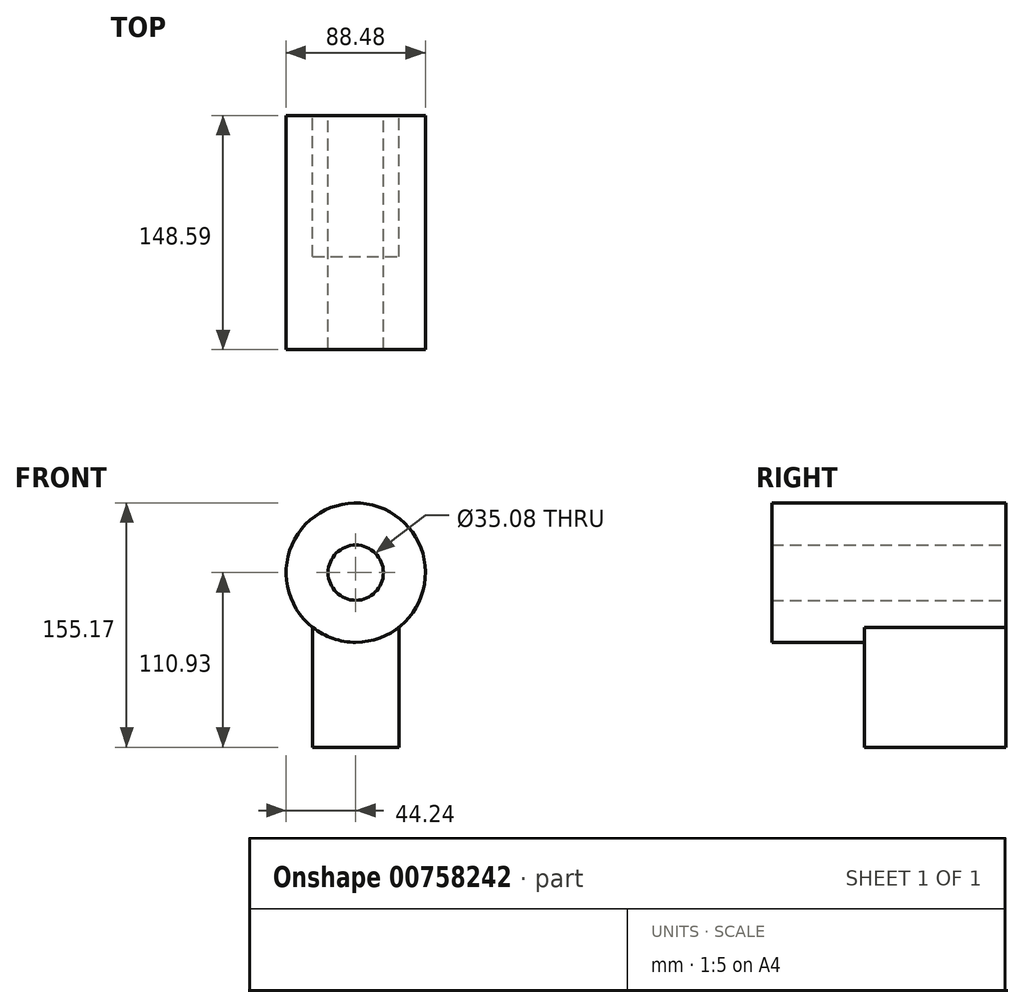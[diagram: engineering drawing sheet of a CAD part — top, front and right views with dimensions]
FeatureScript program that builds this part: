
annotation { "Feature Type Name" : "Feature", "Feature Type Description" : "" }
export const myFeature = defineFeature(function(context is Context, id is Id, definition is map)
    precondition{}
    {
        {
            var Q0;
            Q0=qCreatedBy(makeId("Front.planeOp"),FACE);
            var sketch = newSketch(context, id + "F0", { "sketchPlane" : qUnion([Q0])});
            skCircle(sketch, "E0", {"center": v(0, 0) * mm, "radius": 44.24 * mm});
            skLineSegment(sketch, "E1", {"start": v(-27.4, -34.73) * mm, "end": v(-27.4, -110.93) * mm});
            skLineSegment(sketch, "E2", {"start": v(-27.4, -110.93) * mm, "end": v(27.4, -110.93) * mm});
            skLineSegment(sketch, "E3", {"start": v(27.4, -110.93) * mm, "end": v(27.4, -34.73) * mm});
            skCircle(sketch, "E4", {"center": v(0, 0) * mm, "radius": 17.54 * mm});
            skSolve(sketch);
        }
        {
            var Q0;
            Q0=makeQuery(id+"F0.imprint","IMPRINT",FACE,{"disambiguationData":[TD([[makeQuery(id+"F0.imprint","IMPRINT",EDGE,{"derivedFrom":sQuery(id+"F0.wireOp",EDGE,"E4")}),-1.0]])]});
            extrude(context, id + "F1", {"entities" : qUnion([Q0]), "depth" : 148.6 * mm, "offsetDistance" : 25.4 * mm});
        }
        {
            var Q0;
            Q0 = qSketchRegion(id + "F0", true);
            extrude(context, id + "F2", {"entities" : qUnion([Q0]), "operationType" : NewBodyOperationType.ADD, "depth" : 89.66 * mm, "offsetDistance" : 25.4 * mm});
        }
    });
